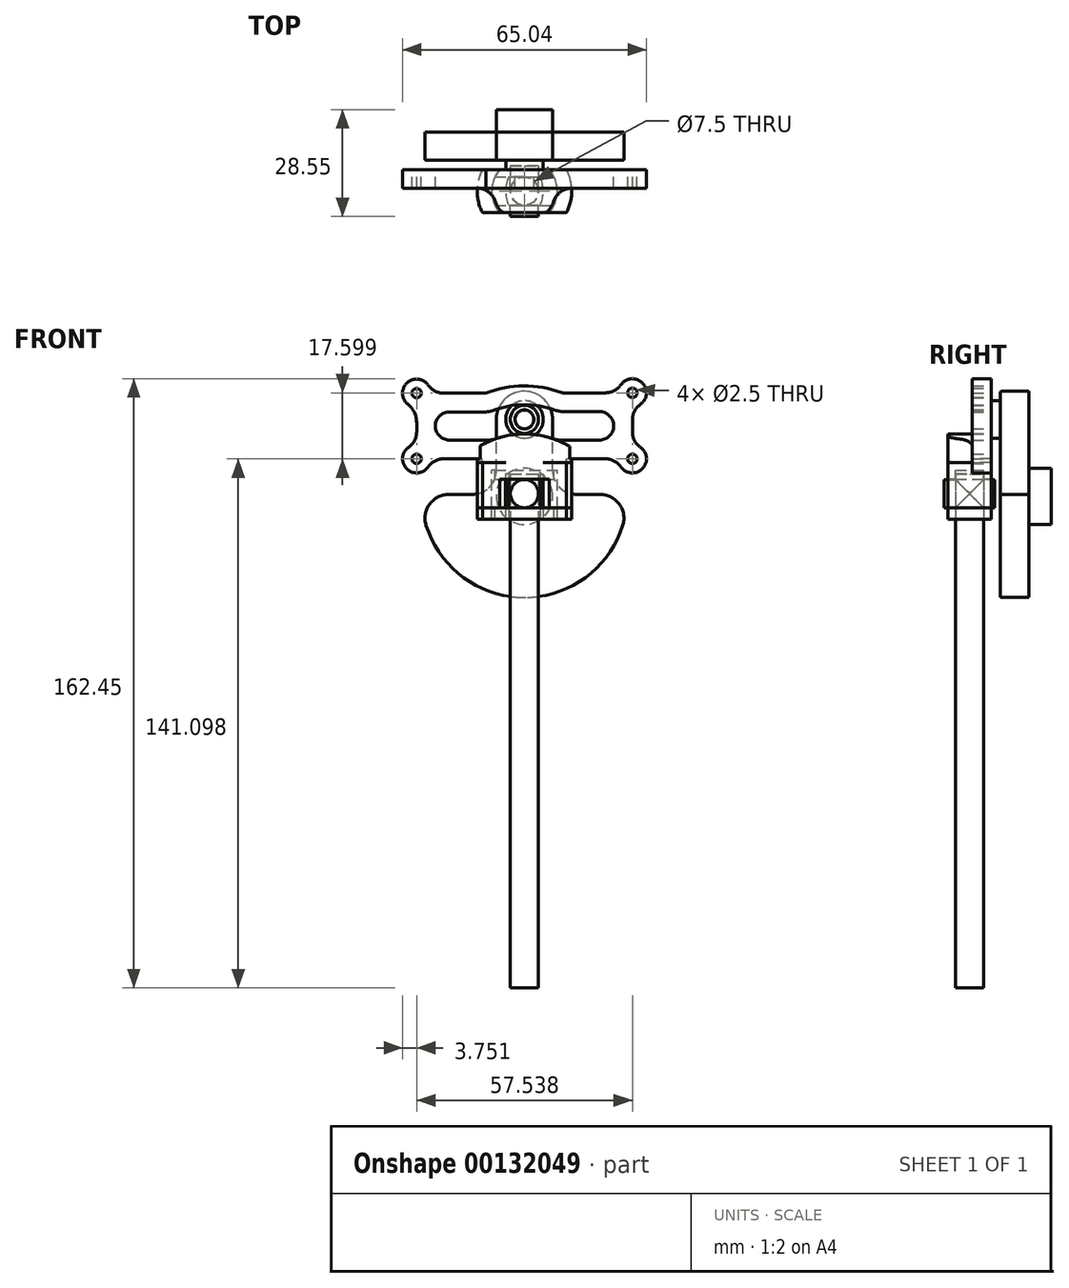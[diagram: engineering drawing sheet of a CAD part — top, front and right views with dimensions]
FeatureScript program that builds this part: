
annotation { "Feature Type Name" : "Feature", "Feature Type Description" : "" }
export const myFeature = defineFeature(function(context is Context, id is Id, definition is map)
    precondition{}
    {
        {
            var Q0;
            Q0=qCreatedBy(makeId("Front.planeOp"),FACE);
            var sketch = newSketch(context, id + "F0", { "sketchPlane" : qUnion([Q0])});
            skArc(sketch, "E0", {"start": v(26.23, -8.26) * mm, "mid": v(0, -27.5) * mm, "end": v(-26.23, -8.26) * mm});
            skLineSegment(sketch, "E1", {"start": v(-7.5, 6.35) * mm, "end": v(-7.5, 20) * mm});
            skLineSegment(sketch, "E2.MirrorCS", {"start": v(7.5, 6.35) * mm, "end": v(7.5, 20) * mm});
            skLineSegment(sketch, "E3", {"start": v(-20.17, 0) * mm, "end": v(-13.85, 0) * mm});
            skLineSegment(sketch, "E4", {"start": v(13.85, 0) * mm, "end": v(20.17, 0) * mm});
            skArc(sketch, "E5", {"start": v(-7.5, 20) * mm, "mid": v(0, 27.5) * mm, "end": v(7.5, 20) * mm});
            skPoint(sketch, "E6.visualSharp", {"position": v(7.5, 0) * mm});
            skArc(sketch, "E6.filletArc", {"start": v(7.5, 6.35) * mm, "mid": v(9.36, 1.86) * mm, "end": v(13.85, 0) * mm});
            skPoint(sketch, "E7.visualSharp", {"position": v(27.5, 0) * mm});
            skArc(sketch, "E7.filletArc", {"start": v(26.23, -8.26) * mm, "mid": v(25.3, -2.6) * mm, "end": v(20.17, 0) * mm});
            skPoint(sketch, "E8.visualSharp", {"position": v(-7.5, 0) * mm});
            skArc(sketch, "E8.filletArc", {"start": v(-13.85, 0) * mm, "mid": v(-9.36, 1.86) * mm, "end": v(-7.5, 6.35) * mm});
            skPoint(sketch, "E9.visualSharp", {"position": v(-27.5, 0) * mm});
            skArc(sketch, "E9.filletArc", {"start": v(-20.17, 0) * mm, "mid": v(-25.3, -2.6) * mm, "end": v(-26.23, -8.26) * mm});
            skCircle(sketch, "E10", {"center": v(0, 20) * mm, "radius": 5 * mm});
            skCircle(sketch, "E11", {"center": v(0, 20) * mm, "radius": 2.5 * mm});
            skSolve(sketch);
        }
        {
            var Q0;
            Q0 = qSketchRegion(id + "F0", true);
            var Q1;
            Q1=makeQuery(id+"F0.imprint","IMPRINT",FACE,{"disambiguationData":[TD([[makeQuery(id+"F0.imprint","IMPRINT",EDGE,{"derivedFrom":sQuery(id+"F0.wireOp",EDGE,"E10")}),1.0]])]});
            var Q2;
            Q2=makeQuery(id+"F0.imprint","IMPRINT",FACE,{"disambiguationData":[TD([[makeQuery(id+"F0.imprint","IMPRINT",EDGE,{"derivedFrom":sQuery(id+"F0.wireOp",EDGE,"E11")}),1.0]])]});
            extrude(context, id + "F1", {"entities" : qUnion([Q0, Q1, Q2]), "oppositeDirection" : true, "depth" : 7.5 * mm});
        }
        {
            var Q0;
            Q0=makeQuery(id+"F0.imprint","IMPRINT",FACE,{"disambiguationData":[TD([[makeQuery(id+"F0.imprint","IMPRINT",EDGE,{"derivedFrom":sQuery(id+"F0.wireOp",EDGE,"E10")}),1.0]])]});
            extrude(context, id + "F2", {"entities" : qUnion([Q0]), "operationType" : NewBodyOperationType.ADD, "depth" : 2.5 * mm});
        }
        {
            var Q0;
            Q0=makeQuery(id+"F0.imprint","IMPRINT",FACE,{"disambiguationData":[TD([[makeQuery(id+"F0.imprint","IMPRINT",EDGE,{"derivedFrom":sQuery(id+"F0.wireOp",EDGE,"E11")}),1.0]])]});
            extrude(context, id + "F3", {"entities" : qUnion([Q0]), "operationType" : NewBodyOperationType.ADD, "depth" : 7.5 * mm});
        }
        {
            var Q0;
            Q0=makeQuery(id+"F1.opExtrude","CAP_EDGE",EDGE,{"disambiguationData":[OSD([sQuery(id+"F0.wireOp",EDGE,"E1")])],"isStart":true});
            var Q1;
            Q1=makeQuery(id+"F1.opExtrude","CAP_EDGE",EDGE,{"disambiguationData":[OSD([sQuery(id+"F0.wireOp",EDGE,"E5")])],"isStart":true});
            fillet(context, id + "F4", {"entities" : qUnion([Q0, Q1]), "radius" : 0.25 * mm, "tangentPropagation" : true, "allowEdgeOverflow" : false});
        }
        {
            var Q0;
            Q0=makeQuery(id+"F1.opExtrude","CAP_FACE",FACE,{"disambiguationData":[OSD([sQuery(id+"F0.wireOp",EDGE,"E0"),sQuery(id+"F0.wireOp",EDGE,"E1"),sQuery(id+"F0.wireOp",EDGE,"E2.MirrorCS"),sQuery(id+"F0.wireOp",EDGE,"E3"),sQuery(id+"F0.wireOp",EDGE,"E4"),sQuery(id+"F0.wireOp",EDGE,"E5"),sQuery(id+"F0.wireOp",EDGE,"E6.filletArc"),sQuery(id+"F0.wireOp",EDGE,"E7.filletArc"),sQuery(id+"F0.wireOp",EDGE,"E8.filletArc"),sQuery(id+"F0.wireOp",EDGE,"E9.filletArc")])],"isStart":false});
            var sketch = newSketch(context, id + "F5", { "sketchPlane" : qUnion([Q0])});
            skCircle(sketch, "E12", {"center": v(0, -0.54) * mm, "radius": 7.5 * mm});
            skSolve(sketch);
        }
        {
            var Q0;
            Q0 = qSketchRegion(id + "F5", true);
            extrude(context, id + "F6", {"entities" : qUnion([Q0]), "operationType" : NewBodyOperationType.ADD, "depth" : 6 * mm});
        }
        {
            var Q0;
            Q0=makeQuery(id+"F2.opExtrude","CAP_FACE",FACE,{"disambiguationData":[OSD([sQuery(id+"F0.wireOp",EDGE,"E10"),sQuery(id+"F0.wireOp",EDGE,"E11")])],"isStart":false});
            var sketch = newSketch(context, id + "F7", { "sketchPlane" : qUnion([Q0])});
            skCircle(sketch, "E13", {"center": v(0, 20) * mm, "radius": 2.52 * mm});
            skCircle(sketch, "E14", {"center": v(0, 20) * mm, "radius": 3.75 * mm});
            skLineSegment(sketch, "E15", {"start": v(1.44, 22.08) * mm, "end": v(3.12, 22.08) * mm});
            skArc(sketch, "E16", {"start": v(8.18, 22.46) * mm, "mid": v(-0.2, 23.9) * mm, "end": v(-8.54, 22.33) * mm});
            skLineSegment(sketch, "E17.trimOffspring", {"start": v(10.36, 22.08) * mm, "end": v(19.99, 22.08) * mm});
            skLineSegment(sketch, "E18.trimOffspring", {"start": v(-10.33, 22) * mm, "end": v(-19.99, 22) * mm});
            skPoint(sketch, "E19.start.orphan", {"position": v(0, 22.08) * mm});
            skPoint(sketch, "E20.visualSharp", {"position": v(-9.36, 22) * mm});
            skArc(sketch, "E20.filletArc", {"start": v(-10.33, 22) * mm, "mid": v(-9.42, 22.08) * mm, "end": v(-8.54, 22.33) * mm});
            skPoint(sketch, "E21.visualSharp", {"position": v(9.17, 22.08) * mm});
            skArc(sketch, "E21.filletArc", {"start": v(8.18, 22.46) * mm, "mid": v(9.25, 22.17) * mm, "end": v(10.36, 22.08) * mm});
            skLineSegment(sketch, "E22", {"start": v(0, 0) * mm, "end": v(0, -7.52) * mm});
            skLineSegment(sketch, "E23", {"start": v(19.99, 14.48) * mm, "end": v(9.69, 14.48) * mm});
            skArc(sketch, "E24", {"start": v(7.63, 14.82) * mm, "mid": v(0, 16.09) * mm, "end": v(-7.63, 14.82) * mm});
            skLineSegment(sketch, "E25.trimOffspring", {"start": v(-9.69, 14.48) * mm, "end": v(-19.99, 14.48) * mm});
            skPoint(sketch, "E26.visualSharp", {"position": v(8.57, 14.48) * mm});
            skArc(sketch, "E26.filletArc", {"start": v(7.63, 14.82) * mm, "mid": v(8.65, 14.56) * mm, "end": v(9.69, 14.48) * mm});
            skPoint(sketch, "E27.visualSharp", {"position": v(-8.57, 14.48) * mm});
            skArc(sketch, "E27.filletArc", {"start": v(-9.69, 14.48) * mm, "mid": v(-8.65, 14.56) * mm, "end": v(-7.63, 14.82) * mm});
            skArc(sketch, "E28", {"start": v(-19.99, 22) * mm, "mid": v(-23.75, 18.24) * mm, "end": v(-19.99, 14.48) * mm});
            skArc(sketch, "E29", {"start": v(19.99, 22.08) * mm, "mid": v(23.79, 18.28) * mm, "end": v(19.99, 14.48) * mm});
            skLineSegment(sketch, "E30.0", {"start": v(-9.69, 4.48) * mm, "end": v(-19.99, 4.48) * mm});
            skLineSegment(sketch, "E31.0", {"start": v(-10.33, 27) * mm, "end": v(-19.99, 27) * mm});
            skArc(sketch, "E32.0", {"start": v(9.9, 27.16) * mm, "mid": v(-0.23, 28.9) * mm, "end": v(-10.33, 27) * mm});
            skArc(sketch, "E33.0", {"start": v(9.9, 27.16) * mm, "mid": v(10.12, 27.1) * mm, "end": v(10.36, 27.08) * mm});
            skLineSegment(sketch, "E34.0", {"start": v(10.36, 27.08) * mm, "end": v(19.99, 27.08) * mm});
            skLineSegment(sketch, "E35", {"start": v(-19.99, 9.48) * mm, "end": v(19.99, 9.48) * mm});
            skLineSegment(sketch, "E36", {"start": v(-19.99, 27) * mm, "end": v(-21.57, 27) * mm});
            skPoint(sketch, "E36.endSnap0", {"position": v(-28.75, 18.24) * mm});
            skArc(sketch, "E37", {"start": v(-25.67, 29.14) * mm, "mid": v(-31.3, 29.74) * mm, "end": v(-31.1, 24.08) * mm});
            skCircle(sketch, "E38", {"center": v(-28.75, 27) * mm, "radius": 1.25 * mm});
            skArc(sketch, "E39", {"start": v(-30.9, 12.56) * mm, "mid": v(-31.4, 6.83) * mm, "end": v(-25.67, 7.34) * mm});
            skCircle(sketch, "E40", {"center": v(-28.75, 9.48) * mm, "radius": 1.25 * mm});
            skLineSegment(sketch, "E41.trimOffspring", {"start": v(-28.75, 19.14) * mm, "end": v(-28.75, 16.66) * mm});
            skLineSegment(sketch, "E42.trimOffspring", {"start": v(-21.57, 9.48) * mm, "end": v(-19.99, 9.48) * mm});
            skPoint(sketch, "E43.visualSharp", {"position": v(-28.75, 23.25) * mm});
            skArc(sketch, "E43.filletArc", {"start": v(-28.75, 19.14) * mm, "mid": v(-29.37, 21.88) * mm, "end": v(-31.1, 24.08) * mm});
            skPoint(sketch, "E44.visualSharp", {"position": v(-28.75, 13.23) * mm});
            skArc(sketch, "E44.filletArc", {"start": v(-30.9, 12.56) * mm, "mid": v(-29.32, 14.34) * mm, "end": v(-28.75, 16.66) * mm});
            skPoint(sketch, "E45.visualSharp", {"position": v(-25, 27) * mm});
            skArc(sketch, "E45.filletArc", {"start": v(-25.67, 29.14) * mm, "mid": v(-23.88, 27.56) * mm, "end": v(-21.57, 27) * mm});
            skPoint(sketch, "E46.visualSharp", {"position": v(-25, 9.48) * mm});
            skArc(sketch, "E46.filletArc", {"start": v(-21.57, 9.48) * mm, "mid": v(-23.88, 8.91) * mm, "end": v(-25.67, 7.34) * mm});
            skLineSegment(sketch, "E47", {"start": v(19.99, 27.08) * mm, "end": v(21.6, 27.08) * mm});
            skPoint(sketch, "E47.endSnap0", {"position": v(28.79, 18.28) * mm});
            skLineSegment(sketch, "E48", {"start": v(28.79, 19.9) * mm, "end": v(28.79, 16.66) * mm});
            skLineSegment(sketch, "E49", {"start": v(21.6, 9.48) * mm, "end": v(19.99, 9.48) * mm});
            skArc(sketch, "E50", {"start": v(30.93, 24) * mm, "mid": v(31.44, 29.73) * mm, "end": v(25.71, 29.22) * mm});
            skCircle(sketch, "E51", {"center": v(28.79, 27.08) * mm, "radius": 1.25 * mm});
            skArc(sketch, "E52", {"start": v(25.71, 7.34) * mm, "mid": v(31.44, 6.83) * mm, "end": v(30.93, 12.56) * mm});
            skCircle(sketch, "E53", {"center": v(28.79, 9.48) * mm, "radius": 1.25 * mm});
            skPoint(sketch, "E54.visualSharp", {"position": v(28.79, 13.23) * mm});
            skArc(sketch, "E54.filletArc", {"start": v(28.79, 16.66) * mm, "mid": v(29.36, 14.34) * mm, "end": v(30.93, 12.56) * mm});
            skPoint(sketch, "E55.visualSharp", {"position": v(25.04, 9.48) * mm});
            skArc(sketch, "E55.filletArc", {"start": v(25.71, 7.34) * mm, "mid": v(23.92, 8.91) * mm, "end": v(21.6, 9.48) * mm});
            skPoint(sketch, "E56.visualSharp", {"position": v(28.79, 23.33) * mm});
            skArc(sketch, "E56.filletArc", {"start": v(30.93, 24) * mm, "mid": v(29.36, 22.21) * mm, "end": v(28.79, 19.9) * mm});
            skPoint(sketch, "E57.visualSharp", {"position": v(25.04, 27.08) * mm});
            skArc(sketch, "E57.filletArc", {"start": v(21.6, 27.08) * mm, "mid": v(23.92, 27.64) * mm, "end": v(25.71, 29.22) * mm});
            skSolve(sketch);
        }
        {
            var Q0;
            Q0=makeQuery(id+"F7.imprint","IMPRINT",FACE,{"disambiguationData":[TD([[makeQuery(id+"F7.imprint","IMPRINT",EDGE,{"derivedFrom":sQuery(id+"F7.wireOp",EDGE,"E13")}),-1.0]])]});
            extrude(context, id + "F8", {"entities" : qUnion([Q0]), "depth" : 5 * mm});
        }
        {
            var Q0;
            Q0 = qSketchRegion(id + "F7", true);
            extrude(context, id + "F9", {"entities" : qUnion([Q0]), "depth" : 5 * mm});
        }
        {
            var Q0;
            Q0=makeQuery(id+"F9.opExtrude","SWEPT_FACE",FACE,{"disambiguationData":[OSD([sQuery(id+"F7.wireOp",EDGE,"E35"),sQuery(id+"F7.wireOp",EDGE,"E42.trimOffspring"),sQuery(id+"F7.wireOp",EDGE,"E49")])]});
            var sketch = newSketch(context, id + "F10", { "sketchPlane" : qUnion([Q0])});
            skCircle(sketch, "E58", {"center": v(0, 8.25) * mm, "radius": 3.75 * mm});
            skArc(sketch, "E59.0", {"start": v(7.82, 10.88) * mm, "mid": v(7.3, 12.09) * mm, "end": v(6.6, 13.2) * mm});
            skLineSegment(sketch, "E60", {"start": v(12.57, 7.48) * mm, "end": v(12.6, 7.48) * mm});
            skPoint(sketch, "E61.newPointB", {"position": v(-21.57, 7.38) * mm});
            skArc(sketch, "E61.filletArc", {"start": v(7.82, 10.88) * mm, "mid": v(9.65, 8.41) * mm, "end": v(12.57, 7.48) * mm});
            skPoint(sketch, "E62.visualSharp", {"position": v(-8.2, 7.42) * mm});
            skArc(sketch, "E62.filletArc", {"start": v(-12.6, 7.45) * mm, "mid": v(-9.66, 8.38) * mm, "end": v(-7.83, 10.86) * mm});
            skArc(sketch, "E63", {"start": v(-12.6, 7.45) * mm, "mid": v(-12.17, 4.9) * mm, "end": v(-11.24, 2.5) * mm});
            skLineSegment(sketch, "E64", {"start": v(-11.24, 2.5) * mm, "end": v(11.24, 2.5) * mm});
            skArc(sketch, "E65.trimOffspring", {"start": v(11.24, 2.5) * mm, "mid": v(12.18, 4.92) * mm, "end": v(12.6, 7.48) * mm});
            skPoint(sketch, "E66.start.orphan", {"position": v(-21.57, 7.5) * mm});
            skPoint(sketch, "E67.orphan", {"position": v(21.6, 7.5) * mm});
            skLineSegment(sketch, "E68.MirrorCS", {"start": v(12.57, -2.48) * mm, "end": v(12.6, -2.48) * mm});
            skLineSegment(sketch, "E69.MirrorCS", {"start": v(-5, 14) * mm, "end": v(5, 14) * mm});
            skArc(sketch, "E70.trimOffspring", {"start": v(-6.6, 13.2) * mm, "mid": v(-7.3, 12.08) * mm, "end": v(-7.83, 10.86) * mm});
            skPoint(sketch, "E71.orphan", {"position": v(11.24, 14) * mm});
            skPoint(sketch, "E72.orphan", {"position": v(-11.24, 14) * mm});
            skPoint(sketch, "E73.visualSharp", {"position": v(-5.92, 14) * mm});
            skArc(sketch, "E73.filletArc", {"start": v(-5, 14) * mm, "mid": v(-5.9, 13.79) * mm, "end": v(-6.6, 13.2) * mm});
            skPoint(sketch, "E74.visualSharp", {"position": v(5.92, 14) * mm});
            skArc(sketch, "E74.filletArc", {"start": v(6.6, 13.2) * mm, "mid": v(5.9, 13.79) * mm, "end": v(5, 14) * mm});
            skSolve(sketch);
        }
        {
            var Q0;
            {var subQ6=sQuery(id+"F10.wireOp",EDGE,"E60");Q0=makeQuery(id+"F10.imprint","IMPRINT",FACE,{"disambiguationData":[TD([[makeQuery(id+"F10.imprint","IMPRINT",EDGE,{"derivedFrom":subQ6}),-1.0]])]});}
            var Q1;
            {var subQ1=sQuery(id+"F10.wireOp",EDGE,"E59.0");Q1=makeQuery(id+"F10.imprint","IMPRINT",FACE,{"disambiguationData":[TD([[makeQuery(id+"F10.imprint","IMPRINT",EDGE,{"derivedFrom":subQ1}),1.0]])]});}
            var Q2;
            {var subQ0=sQuery(id+"F10.wireOp",EDGE,"E58");var subQ1=makeQuery(id+"F9.opExtrude","CAP_EDGE",EDGE,{"disambiguationData":[OSD([sQuery(id+"F7.wireOp",EDGE,"E35"),sQuery(id+"F7.wireOp",EDGE,"E42.trimOffspring"),sQuery(id+"F7.wireOp",EDGE,"E49")])],"isStart":false});var subQ2=makeQuery(id+"F10.imprint","INTERSECT",VERTEX,{"disambiguationData":[OD(0.0)],"derivedFrom":[subQ1,subQ0]});Q2=makeQuery(id+"F10.imprint","IMPRINT",FACE,{"disambiguationData":[TD([[makeQuery(id+"F10.imprint","IMPRINT",EDGE,{"disambiguationData":[TD([[subQ2,-1.0]])],"derivedFrom":subQ0}),1.0]])]});}
            var Q3;
            {var subQ0=sQuery(id+"F10.wireOp",EDGE,"E58");var subQ1=makeQuery(id+"F9.opExtrude","CAP_EDGE",EDGE,{"disambiguationData":[OSD([sQuery(id+"F7.wireOp",EDGE,"E35"),sQuery(id+"F7.wireOp",EDGE,"E42.trimOffspring"),sQuery(id+"F7.wireOp",EDGE,"E49")])],"isStart":false});var subQ2=makeQuery(id+"F10.imprint","INTERSECT",VERTEX,{"disambiguationData":[OD(0.0)],"derivedFrom":[subQ1,subQ0]});Q3=makeQuery(id+"F10.imprint","IMPRINT",FACE,{"disambiguationData":[TD([[makeQuery(id+"F10.imprint","IMPRINT",EDGE,{"disambiguationData":[TD([[subQ2,1.0]])],"derivedFrom":subQ0}),1.0]])]});}
            extrude(context, id + "F11", {"entities" : qUnion([Q0, Q1, Q2, Q3]), "operationType" : NewBodyOperationType.ADD, "depth" : 1 * mm});
        }
        {
            var Q0;
            {var subQ1=sQuery(id+"F10.wireOp",EDGE,"E59.0");Q0=makeQuery(id+"F10.imprint","IMPRINT",FACE,{"disambiguationData":[TD([[makeQuery(id+"F10.imprint","IMPRINT",EDGE,{"derivedFrom":subQ1}),1.0]])]});}
            var Q1;
            {var subQ0=sQuery(id+"F10.wireOp",EDGE,"E58");var subQ1=makeQuery(id+"F9.opExtrude","CAP_EDGE",EDGE,{"disambiguationData":[OSD([sQuery(id+"F7.wireOp",EDGE,"E35"),sQuery(id+"F7.wireOp",EDGE,"E42.trimOffspring"),sQuery(id+"F7.wireOp",EDGE,"E49")])],"isStart":false});var subQ2=makeQuery(id+"F10.imprint","INTERSECT",VERTEX,{"disambiguationData":[OD(0.0)],"derivedFrom":[subQ1,subQ0]});Q1=makeQuery(id+"F10.imprint","IMPRINT",FACE,{"disambiguationData":[TD([[makeQuery(id+"F10.imprint","IMPRINT",EDGE,{"disambiguationData":[TD([[subQ2,-1.0]])],"derivedFrom":subQ0}),1.0]])]});}
            var Q2;
            Q2=makeQuery(id+"F9.opExtrude","SWEPT_FACE",FACE,{"disambiguationData":[OSD([sQuery(id+"F7.wireOp",EDGE,"E24")])]});
            extrude(context, id + "F12", {"entities" : qUnion([Q0, Q1]), "operationType" : NewBodyOperationType.ADD, "endBound" : BoundingType.UP_TO_SURFACE, "oppositeDirection" : true, "endBoundEntityFace" : qUnion([Q2]), "depth" : 20.8 * mm});
        }
        {
            var Q0;
            Q0=makeQuery(id+"F11.opExtrude","CAP_FACE",FACE,{"disambiguationData":[OSD([sQuery(id+"F10.wireOp",EDGE,"E59.0"),sQuery(id+"F10.wireOp",EDGE,"E60"),sQuery(id+"F10.wireOp",EDGE,"E61.filletArc"),sQuery(id+"F10.wireOp",EDGE,"E62.filletArc"),sQuery(id+"F10.wireOp",EDGE,"E63"),sQuery(id+"F10.wireOp",EDGE,"E64"),sQuery(id+"F10.wireOp",EDGE,"E65.trimOffspring"),sQuery(id+"F10.wireOp",EDGE,"E69.MirrorCS"),sQuery(id+"F10.wireOp",EDGE,"E70.trimOffspring"),sQuery(id+"F10.wireOp",EDGE,"E73.filletArc"),sQuery(id+"F10.wireOp",EDGE,"E74.filletArc")])],"isStart":false});
            var sketch = newSketch(context, id + "F13", { "sketchPlane" : qUnion([Q0])});
            skLineSegment(sketch, "E75.bottom", {"start": v(11.21, 2.5) * mm, "end": v(-11.21, 2.5) * mm});
            skLineSegment(sketch, "E75.top", {"start": v(11.21, 14) * mm, "end": v(-11.21, 14) * mm});
            skLineSegment(sketch, "E75.right", {"start": v(-12.6, 8.03) * mm, "end": v(-12.6, 8.47) * mm});
            skArc(sketch, "E76", {"start": v(-11.21, 14) * mm, "mid": v(-12.6, 8.25) * mm, "end": v(-11.21, 2.5) * mm});
            skArc(sketch, "E77.trimOffspring", {"start": v(11.21, 2.5) * mm, "mid": v(12.6, 8.25) * mm, "end": v(11.21, 14) * mm});
            skPoint(sketch, "E78.orphan", {"position": v(12.6, 2.5) * mm});
            skPoint(sketch, "E79.orphan", {"position": v(-12.6, 14) * mm});
            skSolve(sketch);
        }
        {
            var Q0;
            Q0 = qSketchRegion(id + "F13", true);
            extrude(context, id + "F14", {"entities" : qUnion([Q0]), "operationType" : NewBodyOperationType.ADD, "depth" : 2 * mm});
        }
        {
            var Q0;
            Q0=makeQuery(id+"F14.opExtrude","CAP_FACE",FACE,{"disambiguationData":[OSD([sQuery(id+"F13.wireOp",EDGE,"E75.bottom"),sQuery(id+"F13.wireOp",EDGE,"E75.top"),sQuery(id+"F13.wireOp",EDGE,"E76"),sQuery(id+"F13.wireOp",EDGE,"E77.trimOffspring")])],"isStart":false});
            var sketch = newSketch(context, id + "F15", { "sketchPlane" : qUnion([Q0])});
            skLineSegment(sketch, "E80.MirrorCS", {"start": v(-7.88, 4.45) * mm, "end": v(7.88, 4.45) * mm});
            skArc(sketch, "E81", {"start": v(-7.88, 12.05) * mm, "mid": v(-8.75, 8.25) * mm, "end": v(-7.88, 4.45) * mm});
            skArc(sketch, "E82.trimOffspring", {"start": v(7.88, 4.45) * mm, "mid": v(8.75, 8.25) * mm, "end": v(7.88, 12.05) * mm});
            skLineSegment(sketch, "E83", {"start": v(-7.88, 12.05) * mm, "end": v(7.88, 12.05) * mm});
            skSolve(sketch);
        }
        {
            var Q0;
            Q0=makeQuery(id+"F15.imprint","IMPRINT",FACE,{"disambiguationData":[TD([[makeQuery(id+"F15.imprint","IMPRINT",EDGE,{"derivedFrom":sQuery(id+"F15.wireOp",EDGE,"E80.MirrorCS")}),-1.0]])]});
            extrude(context, id + "F16", {"entities" : qUnion([Q0]), "operationType" : NewBodyOperationType.ADD, "depth" : 2.5 * mm});
        }
        {
            var Q0;
            Q0=makeQuery(id+"F16.opExtrude","CAP_FACE",FACE,{"disambiguationData":[OSD([sQuery(id+"F13.wireOp",EDGE,"E75.bottom"),sQuery(id+"F13.wireOp",EDGE,"E75.top"),sQuery(id+"F13.wireOp",EDGE,"E76"),sQuery(id+"F13.wireOp",EDGE,"E77.trimOffspring"),sQuery(id+"F15.wireOp",EDGE,"E80.MirrorCS"),sQuery(id+"F15.wireOp",EDGE,"E81"),sQuery(id+"F15.wireOp",EDGE,"E82.trimOffspring"),sQuery(id+"F15.wireOp",EDGE,"E83")])],"isStart":false});
            var sketch = newSketch(context, id + "F17", { "sketchPlane" : qUnion([Q0])});
            skArc(sketch, "E84", {"start": v(-11.21, 14) * mm, "mid": v(-12.6, 8.25) * mm, "end": v(-11.21, 2.5) * mm});
            skArc(sketch, "E85", {"start": v(-6.6, 14) * mm, "mid": v(-8.75, 8.25) * mm, "end": v(-6.6, 2.5) * mm});
            skLineSegment(sketch, "E86", {"start": v(-11.21, 14) * mm, "end": v(-6.6, 14) * mm});
            skLineSegment(sketch, "E87", {"start": v(-11.21, 2.5) * mm, "end": v(-6.6, 2.5) * mm});
            skArc(sketch, "E88.trimOffspring", {"start": v(6.6, 2.5) * mm, "mid": v(8.75, 8.25) * mm, "end": v(6.6, 14) * mm});
            skArc(sketch, "E89.trimOffspring", {"start": v(11.21, 2.5) * mm, "mid": v(12.6, 8.25) * mm, "end": v(11.21, 14) * mm});
            skLineSegment(sketch, "E90.trimOffspring", {"start": v(6.6, 14) * mm, "end": v(11.21, 14) * mm});
            skLineSegment(sketch, "E91.trimOffspring", {"start": v(6.6, 2.5) * mm, "end": v(11.21, 2.5) * mm});
            skCircle(sketch, "E92", {"center": v(0, 8.25) * mm, "radius": 3.75 * mm});
            skSolve(sketch);
        }
        {
            var Q0;
            Q0=makeQuery(id+"F17.imprint","IMPRINT",FACE,{"disambiguationData":[TD([[makeQuery(id+"F17.imprint","IMPRINT",EDGE,{"derivedFrom":sQuery(id+"F17.wireOp",EDGE,"E89.trimOffspring")}),1.0]])]});
            var Q1;
            Q1=makeQuery(id+"F17.imprint","IMPRINT",FACE,{"disambiguationData":[TD([[makeQuery(id+"F17.imprint","IMPRINT",EDGE,{"derivedFrom":sQuery(id+"F17.wireOp",EDGE,"E84")}),1.0]])]});
            extrude(context, id + "F18", {"entities" : qUnion([Q0, Q1]), "operationType" : NewBodyOperationType.ADD, "depth" : 7.6 * mm});
        }
        {
            var Q0;
            Q0=makeQuery(id+"F18.opExtrude","CAP_FACE",FACE,{"disambiguationData":[OSD([sQuery(id+"F17.wireOp",EDGE,"E84"),sQuery(id+"F17.wireOp",EDGE,"E85"),sQuery(id+"F17.wireOp",EDGE,"E86"),sQuery(id+"F17.wireOp",EDGE,"E87")])],"isStart":false});
            var sketch = newSketch(context, id + "F19", { "sketchPlane" : qUnion([Q0])});
            skArc(sketch, "E93", {"start": v(-7.88, 12.05) * mm, "mid": v(-8.75, 8.25) * mm, "end": v(-7.88, 4.45) * mm});
            skArc(sketch, "E94", {"start": v(-11.21, 14) * mm, "mid": v(-12.6, 8.25) * mm, "end": v(-11.21, 2.5) * mm});
            skLineSegment(sketch, "E95", {"start": v(-11.21, 14) * mm, "end": v(11.21, 14) * mm});
            skLineSegment(sketch, "E96", {"start": v(-11.21, 2.5) * mm, "end": v(11.21, 2.5) * mm});
            skLineSegment(sketch, "E97", {"start": v(-7.88, 12.05) * mm, "end": v(7.88, 12.05) * mm});
            skLineSegment(sketch, "E98.MirrorCS", {"start": v(-7.88, 4.45) * mm, "end": v(7.88, 4.45) * mm});
            skArc(sketch, "E99.trimOffspring", {"start": v(7.88, 4.45) * mm, "mid": v(8.75, 8.25) * mm, "end": v(7.88, 12.05) * mm});
            skArc(sketch, "E100.trimOffspring", {"start": v(11.21, 2.5) * mm, "mid": v(12.6, 8.25) * mm, "end": v(11.21, 14) * mm});
            skCircle(sketch, "E101", {"center": v(0, 8.25) * mm, "radius": 3.75 * mm});
            skSolve(sketch);
        }
        {
            var Q0;
            {var subQ6=sQuery(id+"F19.wireOp",EDGE,"E93");Q0=makeQuery(id+"F19.imprint","IMPRINT",FACE,{"disambiguationData":[TD([[makeQuery(id+"F19.imprint","IMPRINT",EDGE,{"derivedFrom":subQ6}),-1.0]])]});}
            var Q1;
            {var subQ4=sQuery(id+"F19.wireOp",EDGE,"E97");Q1=makeQuery(id+"F19.imprint","IMPRINT",FACE,{"disambiguationData":[TD([[makeQuery(id+"F19.imprint","IMPRINT",EDGE,{"derivedFrom":subQ4}),1.0]])]});}
            extrude(context, id + "F20", {"entities" : qUnion([Q0, Q1]), "depth" : 3 * mm});
        }
        {
            var Q0;
            Q0=makeQuery(id+"F20.opExtrude","CAP_FACE",FACE,{"disambiguationData":[OSD([sQuery(id+"F19.wireOp",EDGE,"E93"),sQuery(id+"F19.wireOp",EDGE,"E94"),sQuery(id+"F19.wireOp",EDGE,"E95"),sQuery(id+"F19.wireOp",EDGE,"E97"),sQuery(id+"F19.wireOp",EDGE,"E96"),sQuery(id+"F19.wireOp",EDGE,"E98.MirrorCS"),sQuery(id+"F19.wireOp",EDGE,"E99.trimOffspring"),sQuery(id+"F19.wireOp",EDGE,"E100.trimOffspring")])],"isStart":false});
            var sketch = newSketch(context, id + "F21", { "sketchPlane" : qUnion([Q0])});
            skCircle(sketch, "E102", {"center": v(0, 8.25) * mm, "radius": 3.75 * mm});
            skArc(sketch, "E103", {"start": v(7.88, 12.05) * mm, "mid": v(8.75, 8.25) * mm, "end": v(7.88, 4.45) * mm, "construction": true});
            skLineSegment(sketch, "E104.bottom", {"start": v(-4.2, 12.05) * mm, "end": v(4.2, 12.05) * mm});
            skLineSegment(sketch, "E104.top", {"start": v(-4.2, 4.45) * mm, "end": v(4.2, 4.45) * mm});
            skArc(sketch, "E105", {"start": v(4.2, 4.45) * mm, "mid": v(5.02, 8.25) * mm, "end": v(4.2, 12.05) * mm});
            skArc(sketch, "E106", {"start": v(-4.2, 12.05) * mm, "mid": v(-5.02, 8.25) * mm, "end": v(-4.2, 4.45) * mm});
            skSolve(sketch);
        }
        {
            var Q0;
            Q0=makeQuery(id+"F21.imprint","IMPRINT",FACE,{"disambiguationData":[TD([[makeQuery(id+"F21.imprint","IMPRINT",EDGE,{"derivedFrom":sQuery(id+"F21.wireOp",EDGE,"E102")}),1.0]])]});
            extrude(context, id + "F22", {"entities" : qUnion([Q0]), "depth" : 125 * mm});
        }
        {
            var Q0;
            Q0 = qSketchRegion(id + "F21", true);
            var Q1;
            Q1=makeQuery(id+"F22.opExtrude","CAP_FACE",FACE,{"disambiguationData":[OSD([sQuery(id+"F21.wireOp",EDGE,"E102")])],"isStart":false});
            extrude(context, id + "F23", {"entities" : qUnion([Q0, Q1]), "operationType" : NewBodyOperationType.ADD, "oppositeDirection" : true, "depth" : 12 * mm});
        }
        {
            var Q0;
            Q0=makeQuery(id+"F23.opExtrude","SWEPT_FACE",FACE,{"disambiguationData":[OSD([sQuery(id+"F21.wireOp",EDGE,"E104.bottom")])]});
            var sketch = newSketch(context, id + "F24", { "sketchPlane" : qUnion([Q0])});
            skCircle(sketch, "E107", {"center": v(0, 0.18) * mm, "radius": 3.75 * mm});
            skPoint(sketch, "E107.first.point", {"position": v(0, 3.93) * mm});
            skPoint(sketch, "E107.second.point", {"position": v(0, -3.57) * mm});
            skPoint(sketch, "E107.third.point", {"position": v(3.75, 0) * mm});
            skSolve(sketch);
        }
        {
            var Q0;
            Q0=makeQuery(id+"F24.imprint","IMPRINT",FACE,{"disambiguationData":[TD([[makeQuery(id+"F24.imprint","IMPRINT",EDGE,{"derivedFrom":sQuery(id+"F24.wireOp",EDGE,"E107")}),1.0]])]});
            extrude(context, id + "F25", {"entities" : qUnion([Q0]), "operationType" : NewBodyOperationType.ADD, "depth" : 3 * mm});
        }
        {
            var Q0;
            Q0 = qSketchRegion(id + "F24", true);
            extrude(context, id + "F26", {"entities" : qUnion([Q0]), "operationType" : NewBodyOperationType.ADD, "oppositeDirection" : true, "depth" : 10.5 * mm});
        }
    });
